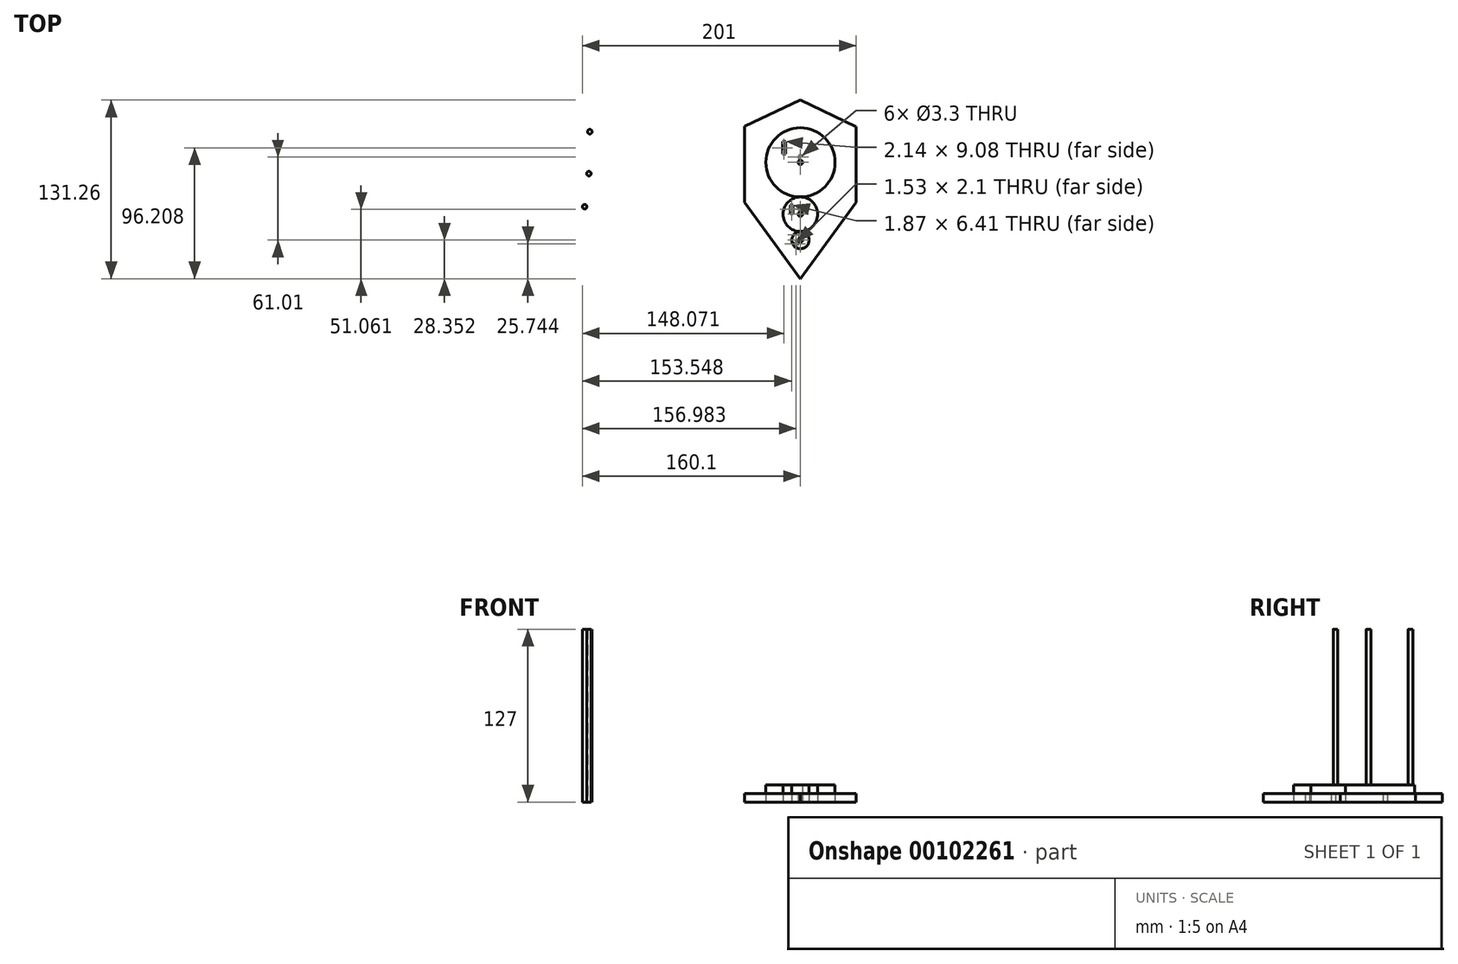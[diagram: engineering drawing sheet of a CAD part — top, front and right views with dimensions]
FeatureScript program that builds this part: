
annotation { "Feature Type Name" : "Feature", "Feature Type Description" : "" }
export const myFeature = defineFeature(function(context is Context, id is Id, definition is map)
    precondition{}
    {
        {
            var Q0;
            Q0=qCreatedBy(makeId("Top.planeOp"),FACE);
            var sketch = newSketch(context, id + "F0", { "sketchPlane" : qUnion([Q0])});
            skLineSegment(sketch, "E0", {"start": v(-40.9, 0) * mm, "end": v(0, -56.27) * mm});
            skLineSegment(sketch, "E1", {"start": v(0, -56.27) * mm, "end": v(40.9, 0) * mm});
            skLineSegment(sketch, "E2", {"start": v(40.9, 0) * mm, "end": v(40.9, 55.36) * mm});
            skLineSegment(sketch, "E3", {"start": v(40.9, 55.36) * mm, "end": v(0, 75) * mm});
            skLineSegment(sketch, "E4", {"start": v(0, 75) * mm, "end": v(-41.09, 55.72) * mm});
            skLineSegment(sketch, "E5", {"start": v(-41.09, 55.72) * mm, "end": v(-40.9, 0) * mm});
            skCircle(sketch, "E6", {"center": v(0, 33.1) * mm, "radius": 1.65 * mm});
            skCircle(sketch, "E7", {"center": v(0, -5) * mm, "radius": 1.65 * mm});
            skCircle(sketch, "E8", {"center": v(0, -24.06) * mm, "radius": 1.65 * mm});
            skSolve(sketch);
        }
        {
            var Q0;
            Q0=qCreatedBy(makeId("Top.planeOp"),FACE);
            var sketch = newSketch(context, id + "F1", { "sketchPlane" : qUnion([Q0])});
            skCircle(sketch, "E9", {"center": v(0, 29.23) * mm, "radius": 25.4 * mm});
            skCircle(sketch, "E10", {"center": v(0, 29.23) * mm, "radius": 1.65 * mm});
            skLineSegment(sketch, "E11.bottom", {"start": v(-13.1, 44.48) * mm, "end": v(-10.96, 44.48) * mm});
            skLineSegment(sketch, "E11.top", {"start": v(-13.1, 35.4) * mm, "end": v(-10.96, 35.4) * mm});
            skLineSegment(sketch, "E11.left", {"start": v(-13.1, 44.48) * mm, "end": v(-13.1, 35.4) * mm});
            skLineSegment(sketch, "E11.right", {"start": v(-10.96, 44.48) * mm, "end": v(-10.96, 35.4) * mm});
            skSolve(sketch);
        }
        {
            var Q0;
            Q0=qCreatedBy(makeId("Top.planeOp"),FACE);
            var sketch = newSketch(context, id + "F2", { "sketchPlane" : qUnion([Q0])});
            skCircle(sketch, "E12", {"center": v(0, -8.87) * mm, "radius": 12.7 * mm});
            skCircle(sketch, "E13", {"center": v(0, -8.87) * mm, "radius": 1.65 * mm});
            skLineSegment(sketch, "E14.bottom", {"start": v(-7.49, -2) * mm, "end": v(-5.62, -2) * mm});
            skLineSegment(sketch, "E14.top", {"start": v(-7.49, -8.42) * mm, "end": v(-5.62, -8.42) * mm});
            skLineSegment(sketch, "E14.left", {"start": v(-7.49, -2) * mm, "end": v(-7.49, -8.42) * mm});
            skLineSegment(sketch, "E14.right", {"start": v(-5.62, -2) * mm, "end": v(-5.62, -8.42) * mm});
            skSolve(sketch);
        }
        {
            var Q0;
            Q0=qCreatedBy(makeId("Top.planeOp"),FACE);
            var sketch = newSketch(context, id + "F3", { "sketchPlane" : qUnion([Q0])});
            skCircle(sketch, "E15", {"center": v(0, -27.92) * mm, "radius": 6.35 * mm});
            skCircle(sketch, "E16", {"center": v(0, -27.92) * mm, "radius": 1.65 * mm});
            skCircle(sketch, "E17", {"center": v(16.62, 27.3) * mm, "radius": 5.1 * mm});
            skLineSegment(sketch, "E18.bottom", {"start": v(-3.88, -29.48) * mm, "end": v(-2.35, -29.48) * mm});
            skLineSegment(sketch, "E18.top", {"start": v(-3.88, -31.58) * mm, "end": v(-2.35, -31.58) * mm});
            skLineSegment(sketch, "E18.left", {"start": v(-3.88, -29.48) * mm, "end": v(-3.88, -31.58) * mm});
            skLineSegment(sketch, "E18.right", {"start": v(-2.35, -29.48) * mm, "end": v(-2.35, -31.58) * mm});
            skSolve(sketch);
        }
        {
            var Q0;
            Q0=makeQuery(id+"F1.imprint","IMPRINT",FACE,{"disambiguationData":[TD([[makeQuery(id+"F1.imprint","IMPRINT",EDGE,{"derivedFrom":sQuery(id+"F1.wireOp",EDGE,"E9")}),1.0]])]});
            extrude(context, id + "F4", {"entities" : qUnion([Q0]), "depth" : 12.7 * mm});
        }
        {
            var Q0;
            Q0=makeQuery(id+"F2.imprint","IMPRINT",FACE,{"disambiguationData":[TD([[makeQuery(id+"F2.imprint","IMPRINT",EDGE,{"derivedFrom":sQuery(id+"F2.wireOp",EDGE,"E12")}),1.0]])]});
            extrude(context, id + "F5", {"entities" : qUnion([Q0]), "operationType" : NewBodyOperationType.ADD, "depth" : 12.7 * mm});
        }
        {
            var Q0;
            Q0=makeQuery(id+"F3.imprint","IMPRINT",FACE,{"disambiguationData":[TD([[makeQuery(id+"F3.imprint","IMPRINT",EDGE,{"derivedFrom":sQuery(id+"F3.wireOp",EDGE,"E15")}),1.0]])]});
            extrude(context, id + "F6", {"entities" : qUnion([Q0]), "operationType" : NewBodyOperationType.ADD, "depth" : 12.7 * mm});
        }
        {
            var Q0;
            Q0=qCreatedBy(makeId("Top.planeOp"),FACE);
            var sketch = newSketch(context, id + "F7", { "sketchPlane" : qUnion([Q0])});
            skCircle(sketch, "E19", {"center": v(-154.68, 51.78) * mm, "radius": 1.65 * mm});
            skSolve(sketch);
        }
        {
            var Q0;
            Q0=qCreatedBy(makeId("Top.planeOp"),FACE);
            var sketch = newSketch(context, id + "F8", { "sketchPlane" : qUnion([Q0])});
            skCircle(sketch, "E20", {"center": v(-155.37, 20.96) * mm, "radius": 1.65 * mm});
            skSolve(sketch);
        }
        {
            var Q0;
            Q0=qCreatedBy(makeId("Top.planeOp"),FACE);
            var sketch = newSketch(context, id + "F9", { "sketchPlane" : qUnion([Q0])});
            skCircle(sketch, "E21", {"center": v(-158.45, -3.35) * mm, "radius": 1.65 * mm});
            skSolve(sketch);
        }
        {
            var Q0;
            Q0=makeQuery(id+"F9.imprint","IMPRINT",FACE,{"disambiguationData":[TD([[makeQuery(id+"F9.imprint","IMPRINT",EDGE,{"derivedFrom":sQuery(id+"F9.wireOp",EDGE,"E21")}),1.0]])]});
            extrude(context, id + "F10", {"entities" : qUnion([Q0]), "depth" : 127 * mm});
        }
        {
            var Q0;
            Q0=makeQuery(id+"F8.imprint","IMPRINT",FACE,{"disambiguationData":[TD([[makeQuery(id+"F8.imprint","IMPRINT",EDGE,{"derivedFrom":sQuery(id+"F8.wireOp",EDGE,"E20")}),1.0]])]});
            extrude(context, id + "F11", {"entities" : qUnion([Q0]), "depth" : 127 * mm});
        }
        {
            var Q0;
            Q0=makeQuery(id+"F7.imprint","IMPRINT",FACE,{"disambiguationData":[TD([[makeQuery(id+"F7.imprint","IMPRINT",EDGE,{"derivedFrom":sQuery(id+"F7.wireOp",EDGE,"E19")}),1.0]])]});
            extrude(context, id + "F12", {"entities" : qUnion([Q0]), "depth" : 127 * mm});
        }
        {
            var Q0;
            Q0=makeQuery(id+"F0.imprint","IMPRINT",FACE,{"disambiguationData":[TD([[makeQuery(id+"F0.imprint","IMPRINT",EDGE,{"derivedFrom":sQuery(id+"F0.wireOp",EDGE,"E0")}),1.0]])]});
            extrude(context, id + "F13", {"entities" : qUnion([Q0]), "depth" : 6.35 * mm});
        }
    });
